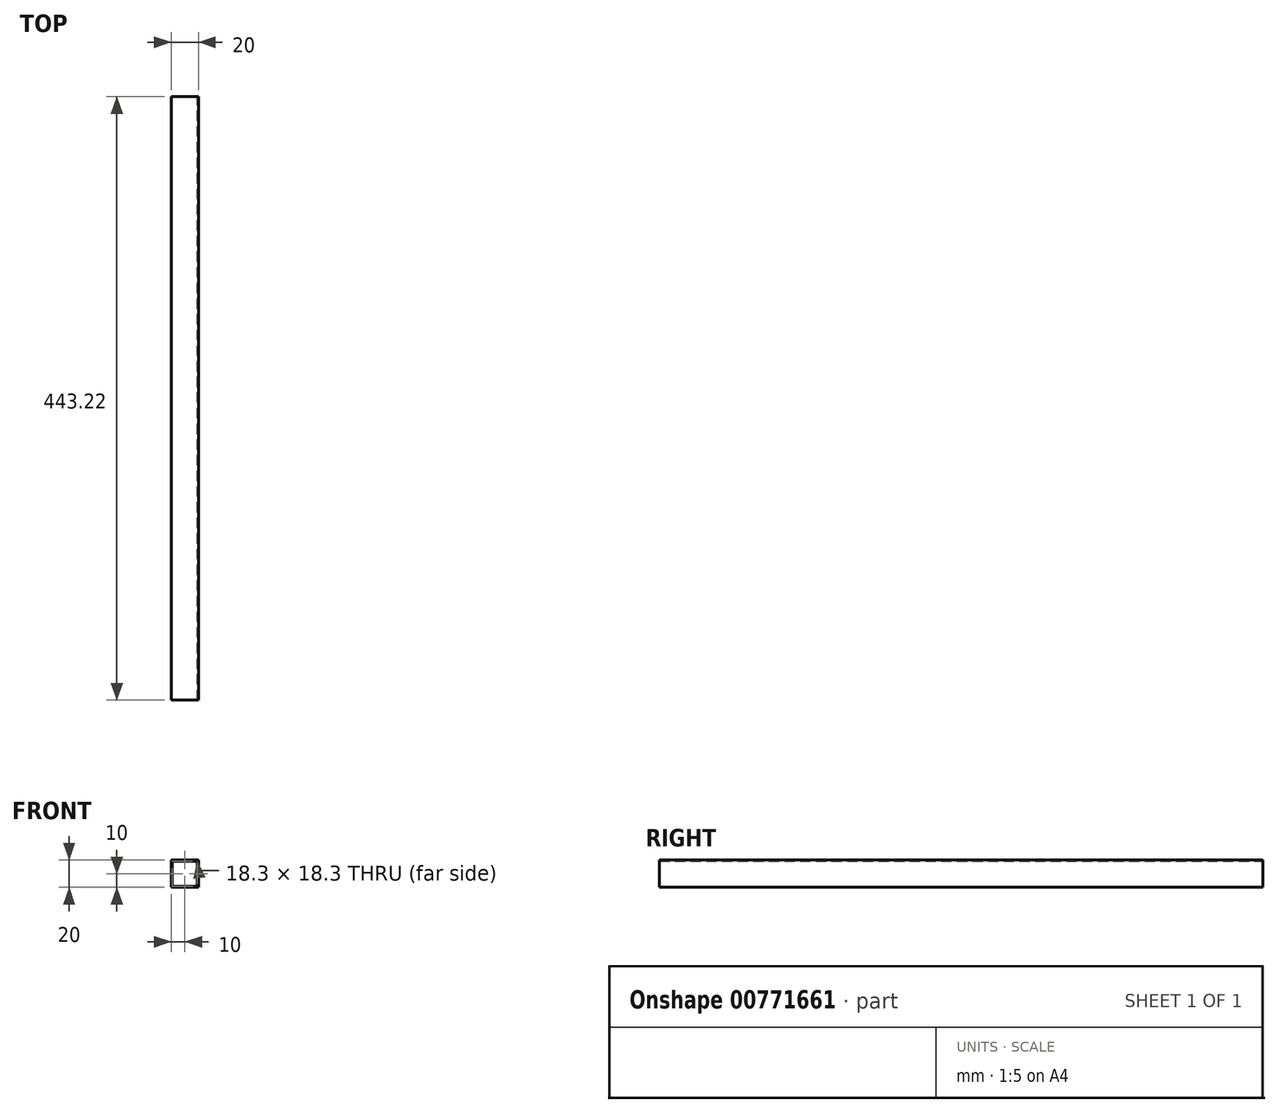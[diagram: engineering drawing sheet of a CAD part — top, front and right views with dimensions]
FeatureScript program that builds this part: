
annotation { "Feature Type Name" : "Feature", "Feature Type Description" : "" }
export const myFeature = defineFeature(function(context is Context, id is Id, definition is map)
    precondition{}
    {
        {
            var Q0;
            Q0=qCreatedBy(makeId("Front.planeOp"),FACE);
            var sketch = newSketch(context, id + "F0", { "sketchPlane" : qUnion([Q0])});
            skLineSegment(sketch, "E0.bottom", {"start": v(10, -10) * mm, "end": v(-10, -10) * mm});
            skLineSegment(sketch, "E0.top", {"start": v(10, 10) * mm, "end": v(-10, 10) * mm});
            skLineSegment(sketch, "E0.left", {"start": v(10, -10) * mm, "end": v(10, 10) * mm});
            skLineSegment(sketch, "E0.right", {"start": v(-10, -10) * mm, "end": v(-10, 10) * mm});
            skPoint(sketch, "E0.middle", {"position": v(0, 0) * mm});
            skLineSegment(sketch, "E1.bottom", {"start": v(9.15, -9.15) * mm, "end": v(-9.15, -9.15) * mm});
            skLineSegment(sketch, "E1.top", {"start": v(9.15, 9.15) * mm, "end": v(-9.15, 9.15) * mm});
            skLineSegment(sketch, "E1.left", {"start": v(9.15, -9.15) * mm, "end": v(9.15, 9.15) * mm});
            skLineSegment(sketch, "E1.right", {"start": v(-9.15, -9.15) * mm, "end": v(-9.15, 9.15) * mm});
            skSolve(sketch);
        }
        {
            var Q0;
            Q0=qSketchRegion(id+"F0",true);
            extrude(context, id + "F1", {"entities" : qUnion([Q0]), "depth" : 443.2 * mm, "offsetDistance" : 25 * mm});
        }
    });
